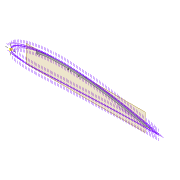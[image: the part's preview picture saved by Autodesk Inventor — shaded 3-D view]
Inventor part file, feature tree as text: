
AUTODESK INVENTOR PART (.ipt)
format: ipt  version: 2022 (Build 260153000, 153)  size: 474,624 bytes
history: native  units: mm
features: sketch x9, projected_geometry x8, extrude x7, shell x1, plane x1, chamfer x1
ambient origin geometry x8: Origin, YZ Plane, XZ Plane, XY Plane, X Axis, Y Axis, Z Axis, Center Point
bodies: Solid1 (feature_tree)
feature tree (27):
  extrude  "Extrusion1"  Depth=4.0mm
  shell  "Shell1"  Thickness=2.0mm
  extrude  "Extrusion8"  Depth=5.9mm
  extrude  "Extrusion3"  Depth=10.0mm TaperAngle=0.0deg
  extrude  "Extrusion4"  Depth=5.0mm
  extrude  "Extrusion5"  Depth=2.5mm
  plane  "Work Plane2"
  extrude  "Extrusion9"  Depth=5.0mm
  chamfer  "Chamfer1"  Distance=2.0mm
  extrude  "Extrusion10"  Depth=20.0mm
  sketch  "Sketch27"  dims[d62=65.0mm]
  sketch  "Sketch28"  dims[d63=5.0mm d64=2.0mm d65=0.0mm d66=2.5mm d67=10.0mm d68=70.0mm d69=20.0mm d70=0.5mm d71=10.0mm d72=0.0mm d73=3.0mm d74=3.0mm d75=2.0mm d76=45.0deg d77=1.0mm d78=0.0mm d79=1.0mm d80=1.0mm d82=1.0mm d83=1.0mm d84=10.0mm d85=0.0mm]
  sketch  "Sketch3"  dims[d0=2.0mm d1=0.0mm d2=4.0mm d7=2.0mm]
  sketch  "Sketch8"  dims[d8=2.0mm d9=5.9mm]
  sketch  "Sketch9"  dims[d13=10.0mm d14=0.0mm d16=10.0mm d17=0.0mm]
  sketch  "Sketch10"  dims[d22=2.0mm d23=0.0mm d32=5.0mm]
  projected_geometry  "Projected Loop4"
  projected_geometry  "Projected Loop10"
  sketch  "Sketch24"  dims[d34=1.6mm d35=2.5mm]
  projected_geometry  "Projected Loop11"
  projected_geometry  "Projected Loop12"
  sketch  "Sketch25"  dims[d37=5.0mm d38=1.6mm]
  projected_geometry  "Projected Loop13"
  sketch  "Sketch26"  dims[d40=2.5mm]
  projected_geometry  "Project Cut Edges1"
  projected_geometry  "Project Cut Edges2"
  projected_geometry  "Project Cut Edges3"
